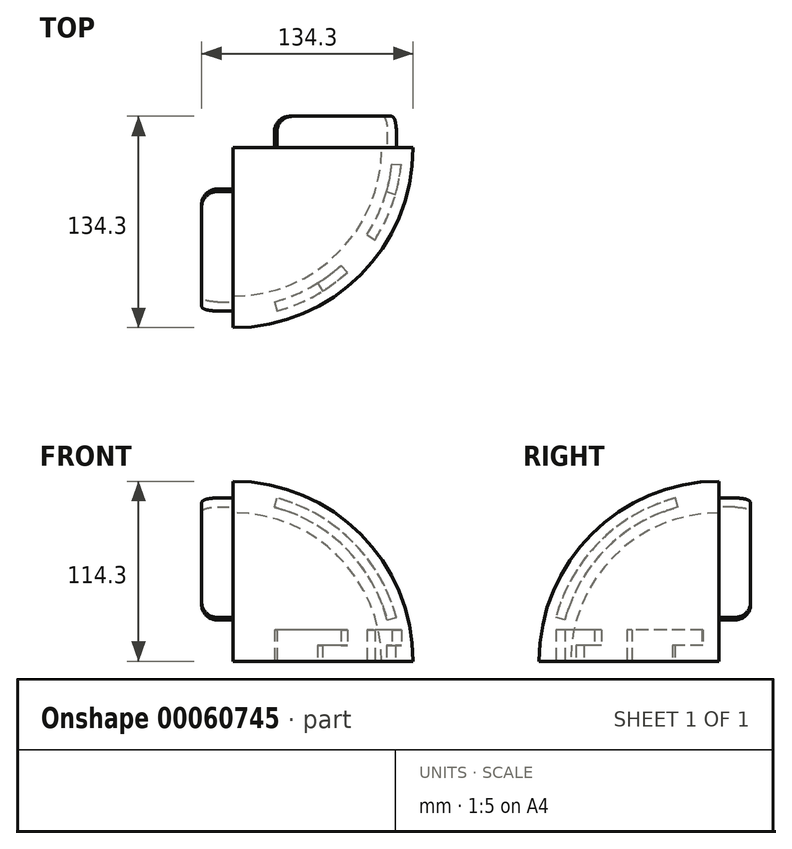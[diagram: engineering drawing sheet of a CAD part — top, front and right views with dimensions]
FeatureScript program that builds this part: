
annotation { "Feature Type Name" : "Feature", "Feature Type Description" : "" }
export const myFeature = defineFeature(function(context is Context, id is Id, definition is map)
    precondition{}
    {
        {
            var Q0;
            Q0=qCreatedBy(makeId("Right.planeOp"),FACE);
            var sketch = newSketch(context, id + "F0", { "sketchPlane" : qUnion([Q0])});
            skArc(sketch, "E0", {"start": v(0, 114.3) * mm, "mid": v(-80.82, 80.82) * mm, "end": v(-114.3, 0) * mm});
            skArc(sketch, "E1", {"start": v(0, 94.3) * mm, "mid": v(-66.68, 66.68) * mm, "end": v(-94.3, 0) * mm});
            skLineSegment(sketch, "E2", {"start": v(0, 94.3) * mm, "end": v(0, 114.3) * mm});
            skLineSegment(sketch, "E3", {"start": v(-94.3, 0) * mm, "end": v(-114.3, 0) * mm});
            skSolve(sketch);
        }
        {
            var Q0;
            Q0=makeQuery(id+"F0.imprint","IMPRINT",FACE,{"disambiguationData":[TD([[makeQuery(id+"F0.imprint","IMPRINT",EDGE,{"derivedFrom":sQuery(id+"F0.wireOp",EDGE,"E0")}),1.0]])]});
            var Q1;
            Q1=sQuery(id+"F0.wireOp",EDGE,"E2");
            revolve(context, id + "F1", {"entities" : qUnion([Q0]), "axis" : qUnion([Q1]), "revolveType" : RevolveType.ONE_DIRECTION, "angle" : 90 * degree});
        }
        {
            var Q0;
            Q0=makeQuery(id+"F1.opRevolve","CAP_FACE",FACE,{"disambiguationData":[OSD([sQuery(id+"F0.wireOp",EDGE,"E0"),sQuery(id+"F0.wireOp",EDGE,"E1"),sQuery(id+"F0.wireOp",EDGE,"E2"),sQuery(id+"F0.wireOp",EDGE,"E3")])],"isStart":false});
            var sketch = newSketch(context, id + "F2", { "sketchPlane" : qUnion([Q0])});
            skArc(sketch, "E4", {"start": v(-27.77, 103.64) * mm, "mid": v(-75.87, 75.87) * mm, "end": v(-103.64, 27.77) * mm});
            skArc(sketch, "E5", {"start": v(-26.22, 97.85) * mm, "mid": v(-71.63, 71.63) * mm, "end": v(-97.85, 26.22) * mm});
            skLineSegment(sketch, "E6", {"start": v(0, 0) * mm, "end": v(-27.77, 103.64) * mm});
            skLineSegment(sketch, "E7", {"start": v(-97.85, 26.22) * mm, "end": v(-103.64, 27.77) * mm});
            skSolve(sketch);
        }
        {
            var Q0;
            Q0=makeQuery(id+"F2.imprint","IMPRINT",FACE,{"disambiguationData":[TD([[makeQuery(id+"F2.imprint","IMPRINT",EDGE,{"derivedFrom":sQuery(id+"F2.wireOp",EDGE,"E4")}),1.0]])]});
            extrude(context, id + "F3", {"entities" : qUnion([Q0]), "operationType" : NewBodyOperationType.ADD, "depth" : 20 * mm});
        }
        {
            var Q0;
            Q0=makeQuery(id+"F0.imprint","IMPRINT",FACE,{"disambiguationData":[TD([[makeQuery(id+"F0.imprint","IMPRINT",EDGE,{"derivedFrom":sQuery(id+"F0.wireOp",EDGE,"E0")}),1.0]])]});
            var sketch = newSketch(context, id + "F4", { "sketchPlane" : qUnion([Q0])});
            skArc(sketch, "E8.0", {"start": v(-26.22, 97.85) * mm, "mid": v(-71.63, 71.63) * mm, "end": v(-97.85, 26.22) * mm});
            skArc(sketch, "E9.0", {"start": v(-27.77, 103.64) * mm, "mid": v(-75.87, 75.87) * mm, "end": v(-103.64, 27.77) * mm});
            skLineSegment(sketch, "E10", {"start": v(-26.22, 97.85) * mm, "end": v(-27.77, 103.64) * mm});
            skLineSegment(sketch, "E11", {"start": v(-97.85, 26.22) * mm, "end": v(-103.64, 27.77) * mm});
            skSolve(sketch);
        }
        {
            var Q0;
            Q0=makeQuery(id+"F4.imprint","IMPRINT",FACE,{"disambiguationData":[TD([[makeQuery(id+"F4.imprint","IMPRINT",EDGE,{"derivedFrom":sQuery(id+"F4.wireOp",EDGE,"E8.0")}),-1.0]])]});
            extrude(context, id + "F5", {"entities" : qUnion([Q0]), "operationType" : NewBodyOperationType.ADD, "oppositeDirection" : true, "depth" : 20 * mm});
        }
        {
            var Q0;
            Q0=makeQuery(id+"F5.boolean.opBoolean","MERGE",FACE,{"derivedFrom":[makeQuery(id+"F3.boolean.opBoolean","MERGE",FACE,{"derivedFrom":[makeQuery(id+"F1.opRevolve","SWEPT_FACE",FACE,{"disambiguationData":[OSD([sQuery(id+"F0.wireOp",EDGE,"E3")])]}),makeQuery(id+"F3.opExtrude","SWEPT_FACE",FACE,{"disambiguationData":[OSD([sQuery(id+"F2.wireOp",EDGE,"tj54Cu89-9J1S-AJKw-QeEM-ljXHSpR1f2pj")])]})]}),makeQuery(id+"F5.opExtrude","SWEPT_FACE",FACE,{"disambiguationData":[OSD([sQuery(id+"F4.wireOp",EDGE,"EMUQLBOC-9Rso-lLbz-JRUg-i4oPmn0DbPj1")])]})]});
            var sketch = newSketch(context, id + "F6", { "sketchPlane" : qUnion([Q0])});
            skArc(sketch, "E12", {"start": v(97.38, 27.92) * mm, "mid": v(92.18, 42) * mm, "end": v(84.96, 55.17) * mm});
            skArc(sketch, "E13", {"start": v(103.14, 29.58) * mm, "mid": v(97.64, 44.5) * mm, "end": v(89.99, 58.44) * mm});
            skLineSegment(sketch, "E14", {"start": v(26.22, 97.85) * mm, "end": v(27.77, 103.64) * mm});
            skLineSegment(sketch, "E15", {"start": v(53.68, 85.9) * mm, "end": v(56.86, 91) * mm});
            skLineSegment(sketch, "E16", {"start": v(84.96, 55.17) * mm, "end": v(89.99, 58.44) * mm});
            skLineSegment(sketch, "E17", {"start": v(97.38, 27.92) * mm, "end": v(103.14, 29.58) * mm});
            skArc(sketch, "E18.trimOffspring", {"start": v(53.68, 85.9) * mm, "mid": v(40.4, 92.9) * mm, "end": v(26.22, 97.85) * mm});
            skArc(sketch, "E19.trimOffspring", {"start": v(56.86, 91) * mm, "mid": v(42.79, 98.4) * mm, "end": v(27.77, 103.64) * mm});
            skSolve(sketch);
        }
        {
            var Q0;
            Q0=makeQuery(id+"F6.imprint","IMPRINT",FACE,{"disambiguationData":[TD([[makeQuery(id+"F6.imprint","IMPRINT",EDGE,{"derivedFrom":sQuery(id+"F6.wireOp",EDGE,"E14")}),-1.0]])]});
            var Q1;
            Q1=makeQuery(id+"F6.imprint","IMPRINT",FACE,{"disambiguationData":[TD([[makeQuery(id+"F6.imprint","IMPRINT",EDGE,{"derivedFrom":sQuery(id+"F6.wireOp",EDGE,"E12")}),-1.0]])]});
            extrude(context, id + "F7", {"entities" : qUnion([Q0, Q1]), "operationType" : NewBodyOperationType.REMOVE, "oppositeDirection" : true, "depth" : 20 * mm});
        }
        {
            var Q0;
            Q0=makeQuery(id+"F3.opExtrude","CAP_EDGE",EDGE,{"disambiguationData":[OSD([sQuery(id+"F2.wireOp",EDGE,"E7")])],"isStart":false});
            var Q1;
            Q1=makeQuery(id+"F3.opExtrude","CAP_EDGE",EDGE,{"disambiguationData":[OSD([sQuery(id+"F2.wireOp",EDGE,"E6")])],"isStart":false});
            var Q2;
            Q2=makeQuery(id+"F5.opExtrude","CAP_EDGE",EDGE,{"disambiguationData":[OSD([sQuery(id+"F4.wireOp",EDGE,"E10")])],"isStart":false});
            var Q3;
            Q3=makeQuery(id+"F5.opExtrude","CAP_EDGE",EDGE,{"disambiguationData":[OSD([sQuery(id+"F4.wireOp",EDGE,"E11")])],"isStart":false});
            fillet(context, id + "F8", {"entities" : qUnion([Q0, Q1, Q2, Q3]), "radius" : 10 * mm, "tangentPropagation" : true, "allowEdgeOverflow" : false});
        }
        {
            var Q0;
            Q0=makeQuery(id+"F6.imprint","IMPRINT",FACE,{"disambiguationData":[TD([[makeQuery(id+"F6.imprint","IMPRINT",EDGE,{"derivedFrom":sQuery(id+"F6.wireOp",EDGE,"E12")}),1.0]])]});
            cPlane(context, id + "F9", {"entities" : qUnion([Q0]), "cplaneType" : CPlaneType.OFFSET, "offset" : 10 * mm, "oppositeDirection" : true, "width" : 150 * mm, "height" : 150 * mm});
        }
        {
            var Q0;
            Q0=qCreatedBy(id+"F9.planeOp",FACE);
            var sketch = newSketch(context, id + "F10", { "sketchPlane" : qUnion([Q0])});
            skArc(sketch, "E20", {"start": v(100.79, 10.2) * mm, "mid": v(99.48, 19.14) * mm, "end": v(97.38, 27.92) * mm});
            skArc(sketch, "E21", {"start": v(106.76, 10.77) * mm, "mid": v(105.37, 20.25) * mm, "end": v(103.14, 29.58) * mm});
            skLineSegment(sketch, "E22", {"start": v(0, 0) * mm, "end": v(0.33, 0.52) * mm});
            skLineSegment(sketch, "E23", {"start": v(0, 0) * mm, "end": v(0.5, 0.54) * mm});
            skLineSegment(sketch, "E24", {"start": v(0, 0) * mm, "end": v(2.58, 0.74) * mm});
            skLineSegment(sketch, "E25", {"start": v(-5.11, 0) * mm, "end": v(2.58, 0.74) * mm});
            skLineSegment(sketch, "E26.trimOffspring", {"start": v(53.68, 85.9) * mm, "end": v(56.86, 91) * mm});
            skLineSegment(sketch, "E27.trimOffspring", {"start": v(68.44, 74.69) * mm, "end": v(72.5, 79.1) * mm});
            skLineSegment(sketch, "E28.trimOffspring", {"start": v(97.38, 27.92) * mm, "end": v(103.14, 29.58) * mm});
            skLineSegment(sketch, "E29.trimOffspring", {"start": v(100.79, 10.2) * mm, "end": v(106.76, 10.77) * mm});
            skArc(sketch, "E30.trimOffspring", {"start": v(68.44, 74.69) * mm, "mid": v(61.32, 80.64) * mm, "end": v(53.68, 85.9) * mm});
            skArc(sketch, "E31.trimOffspring", {"start": v(72.5, 79.1) * mm, "mid": v(64.95, 85.41) * mm, "end": v(56.86, 91) * mm});
            skSolve(sketch);
        }
        {
            var Q0;
            Q0 = qSketchRegion(id + "F10", true);
            extrude(context, id + "F11", {"entities" : qUnion([Q0]), "operationType" : NewBodyOperationType.REMOVE, "oppositeDirection" : true, "depth" : 10 * mm});
        }
    });
